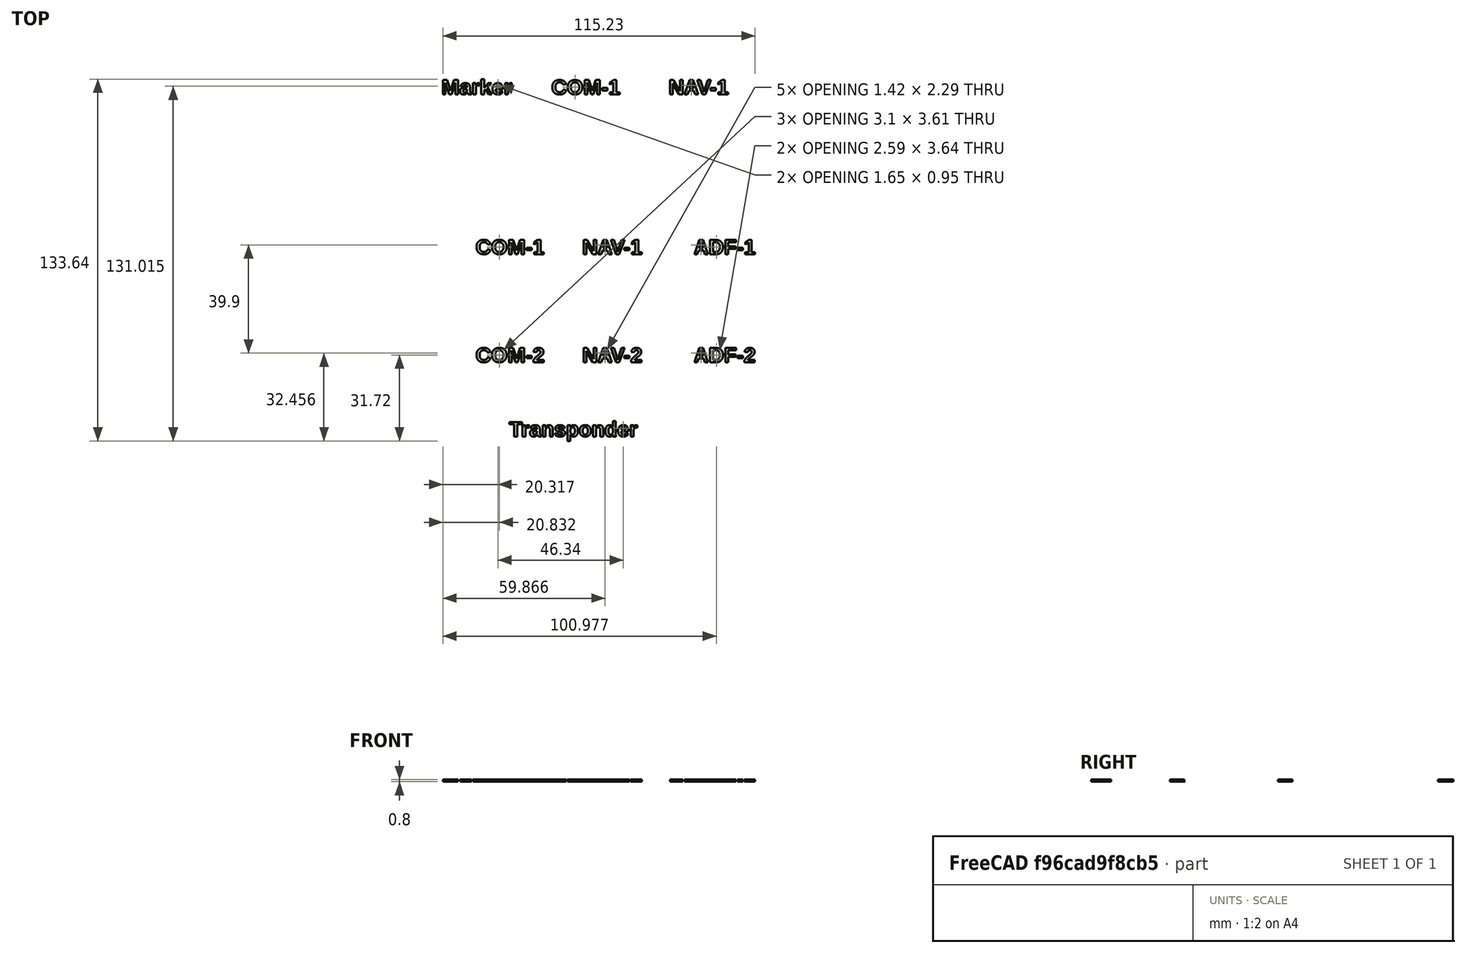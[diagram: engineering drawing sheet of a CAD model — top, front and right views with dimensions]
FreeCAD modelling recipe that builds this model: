
FCSTD DOCUMENT  (FreeCAD 0.17R13522 (Git))
Label: letras_izquierda
License: CreativeCommons Attribution-ShareAlike
LicenseURL: http://creativecommons.org/licenses/by-sa/4.0/
objects: Part::Cut×12, Part::Feature×10, Part::Box×6, Part::Fuse×3
note: 31 computed .brp shape members not serialized (recipe doc carries the construction recipe); baked Part::Feature solids carry a one-line shape summary decoded from their .brp

FEATURE [Part::Feature] Cut001001001002003001008002002033001001001001001001001002001001002001045002003011001  label="Cut001001001002003001008002002033001001001001001001001002001001002001045002003012"
  shape: bbox 135 x 157.9 x 19 mm, 1324 faces (baked)
FEATURE [Part::Box] Box  label="Cube"
  AttacherType = Attacher::AttachEngine3D
  Height = 10
  Length = 130
  Placement = pos=(0,-4,-104) rot=(0,0,1;0rad)
  Width = 157.85
FEATURE [Part::Cut] Cut
  Base = -> Box
  Refine = true
  Tool = -> Cut001001001002003001008002002033001001001001001001001002001001002001045002003011001
FEATURE [Part::Box] Box001  label="Cube001"
  AttacherType = Attacher::AttachEngine3D
  Height = 10
  Length = 130
  Placement = pos=(0,-4,-103.1) rot=(0,0,1;0rad)
  Width = 157.85
FEATURE [Part::Cut] Cut001001001002003001008002002033001001001001001001001002001001002001045002003011002
  Base = -> Cut
  Refine = true
  Tool = -> Box001
FEATURE [Part::Box] Box002  label="Cube002"
  AttacherType = Attacher::AttachEngine3D
  Height = 100
  Length = 140
  Placement = pos=(-5,-8,-118) rot=(0,0,1;0rad)
  Width = 10
FEATURE [Part::Feature] Box002001  label="Cube003"
  Placement = pos=(-5,13,-118) rot=(0,0,1;0rad)
  shape: bbox 140 x 10 x 100 mm, 6 faces (baked)
FEATURE [Part::Feature] Box002001001  label="Cube004"
  Placement = pos=(-5,20,-118) rot=(0,0,1;0rad)
  shape: bbox 140 x 10 x 100 mm, 6 faces (baked)
FEATURE [Part::Fuse] Fusion
  Base = -> Box002001
  Refine = true
  Tool = -> Box002001001
FEATURE [Part::Feature] Fusion001
  Placement = pos=(0,27,0) rot=(0,0,1;0rad)
  shape: bbox 140 x 17 x 100 mm, 6 faces (baked)
FEATURE [Part::Feature] Fusion001001  label="Fusion002"
  Placement = pos=(0,40,0) rot=(0,0,1;0rad)
  shape: bbox 140 x 17 x 100 mm, 6 faces (baked)
FEATURE [Part::Fuse] Fusion001002
  Base = -> Fusion001
  Refine = true
  Tool = -> Fusion001001
FEATURE [Part::Feature] Fusion001002001  label="Fusion001003"
  Placement = pos=(0,40,0) rot=(0,0,1;0rad)
  shape: bbox 140 x 30 x 100 mm, 6 faces (baked)
FEATURE [Part::Feature] Fusion001002001001  label="Fusion001004"
  Placement = pos=(0,58,0) rot=(0,0,1;0rad)
  shape: bbox 140 x 30 x 100 mm, 6 faces (baked)
FEATURE [Part::Fuse] Fusion001002001002
  Base = -> Fusion001002001
  Refine = true
  Tool = -> Fusion001002001001
FEATURE [Part::Feature] Fusion001002001003
  Placement = pos=(0,98,0) rot=(0,0,1;0rad)
  shape: bbox 140 x 30 x 100 mm, 6 faces (baked)
FEATURE [Part::Cut] Cut001001001002003001008002002033001001001001001001001002001001002001045002003011003
  Base = -> Cut001001001002003001008002002033001001001001001001001002001001002001045002003011002
  Refine = true
  Tool = -> Fusion001002001003
FEATURE [Part::Cut] Cut001001001002003001008002002033001001001001001001001002001001002001045002003011004
  Base = -> Cut001001001002003001008002002033001001001001001001001002001001002001045002003011003
  Refine = true
  Tool = -> Box002
FEATURE [Part::Cut] Cut001001001002003001008002002033001001001001001001001002001001002001045002003011005
  Base = -> Cut001001001002003001008002002033001001001001001001001002001001002001045002003011004
  Refine = true
  Tool = -> Fusion
FEATURE [Part::Cut] Cut001001001002003001008002002033001001001001001001001002001001002001045002003011006
  Base = -> Cut001001001002003001008002002033001001001001001001001002001001002001045002003011005
  Refine = true
  Tool = -> Fusion001002
FEATURE [Part::Cut] Cut001001001002003001008002002033001001001001001001001002001001002001045002003011007
  Base = -> Cut001001001002003001008002002033001001001001001001001002001001002001045002003011006
  Refine = true
  Tool = -> Fusion001002001002
FEATURE [Part::Box] Box002001002  label="Cube005"
  AttacherType = Attacher::AttachEngine3D
  Height = 10
  Length = 10
  Placement = pos=(33,130,-108) rot=(0,0,1;0rad)
  Width = 10
FEATURE [Part::Feature] Box002001002001  label="Cube006"
  Placement = pos=(73,130,-108) rot=(0,0,1;0rad)
  shape: bbox 10 x 10 x 10 mm, 6 faces (baked)
FEATURE [Part::Feature] Box002001002001001  label="Cube007"
  Placement = pos=(111,130,-108) rot=(0,0,1;0rad)
  shape: bbox 10 x 10 x 10 mm, 6 faces (baked)
FEATURE [Part::Cut] Cut001001001002003001008002002033001001001001001001001002001001002001045002003011008
  Base = -> Cut001001001002003001008002002033001001001001001001001002001001002001045002003011007
  Refine = true
  Tool = -> Box002001002001001
FEATURE [Part::Cut] Cut001001001002003001008002002033001001001001001001001002001001002001045002003011009
  Base = -> Cut001001001002003001008002002033001001001001001001001002001001002001045002003011008
  Refine = true
  Tool = -> Box002001002
FEATURE [Part::Cut] Cut001001001002003001008002002033001001001001001001001002001001002001045002003011010
  Base = -> Cut001001001002003001008002002033001001001001001001001002001001002001045002003011009
  Refine = true
  Tool = -> Box002001002001
FEATURE [Part::Box] Box002001002001002  label="Cube008"
  AttacherType = Attacher::AttachEngine3D
  Height = 10
  Length = 20
  Placement = pos=(114,37.8,-107) rot=(0,0,1;0rad)
  Width = 10
FEATURE [Part::Cut] Cut001001001002003001008002002033001001001001001001001002001001002001045002003011011
  Base = -> Cut001001001002003001008002002033001001001001001001001002001001002001045002003011010
  Refine = true
  Tool = -> Box002001002001002
FEATURE [Part::Box] Box002001002001003  label="Cube009"
  AttacherType = Attacher::AttachEngine3D
  Height = 10
  Length = 200
  Placement = pos=(0,0,-113.9) rot=(0,0,1;0rad)
  Width = 200
FEATURE [Part::Cut] Cut001001001002003001008002002033001001001001001001001002001001002001045002003011012  label="letras_izquierda"
  Base = -> Cut001001001002003001008002002033001001001001001001001002001001002001045002003011011
  Refine = true
  Tool = -> Box002001002001003
